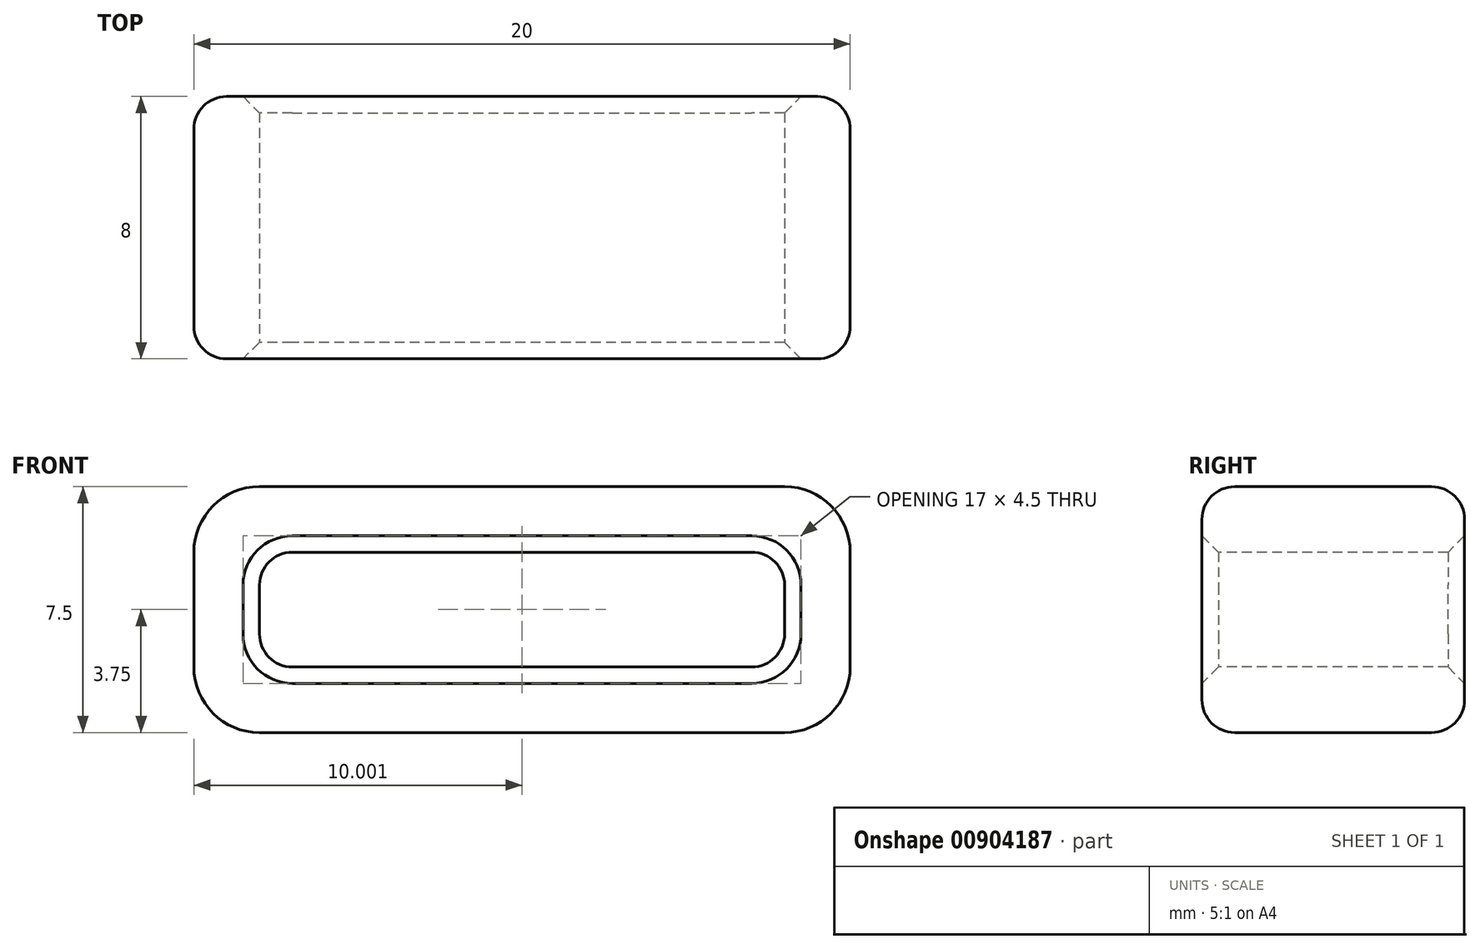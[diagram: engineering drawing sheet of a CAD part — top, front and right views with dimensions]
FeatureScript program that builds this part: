
annotation { "Feature Type Name" : "Feature", "Feature Type Description" : "" }
export const myFeature = defineFeature(function(context is Context, id is Id, definition is map)
    precondition{}
    {
        {
            var Q0;
            Q0=qCreatedBy(makeId("Top.planeOp"),FACE);
            var sketch = newSketch(context, id + "F0", { "sketchPlane" : qUnion([Q0])});
            skLineSegment(sketch, "E0.bottom", {"start": v(5.5, 5.36) * mm, "end": v(25.5, 5.36) * mm});
            skLineSegment(sketch, "E0.top", {"start": v(5.5, -2.64) * mm, "end": v(25.5, -2.64) * mm});
            skLineSegment(sketch, "E0.left", {"start": v(5.5, 5.36) * mm, "end": v(5.5, -2.64) * mm});
            skLineSegment(sketch, "E0.right", {"start": v(25.5, 5.36) * mm, "end": v(25.5, -2.64) * mm});
            skSolve(sketch);
        }
        {
            var Q0;
            Q0 = qSketchRegion(id + "F0", true);
            extrude(context, id + "F1", {"entities" : qUnion([Q0]), "depth" : 7.5 * mm, "offsetDistance" : 25 * mm});
        }
        {
            var Q0;
            Q0=makeQuery(id+"F1.opExtrude","SWEPT_FACE",FACE,{"disambiguationData":[OSD([sQuery(id+"F0.wireOp",EDGE,"E0.top")])]});
            var Q1;
            Q1=makeQuery(id+"F1.opExtrude","SWEPT_BODY",BODY,{"disambiguationData":[OSD([sQuery(id+"F0.wireOp",EDGE,"E0.bottom"),sQuery(id+"F0.wireOp",EDGE,"E0.top"),sQuery(id+"F0.wireOp",EDGE,"E0.left"),sQuery(id+"F0.wireOp",EDGE,"E0.right")])]});
            shell(context, id + "F2", {"entities" : qUnion([Q0]), "parts" : qUnion([Q1]), "thickness" : 2 * mm});
        }
        {
            var Q0;
            Q0=makeQuery(id+"F2.opShell","OFFSET_FACE",FACE,{"disambiguationData":[OSD([sQuery(id+"F0.wireOp",EDGE,"E0.bottom")])]});
            extrude(context, id + "F3", {"entities" : qUnion([Q0]), "operationType" : NewBodyOperationType.REMOVE, "oppositeDirection" : true, "depth" : 25 * mm, "offsetDistance" : 25 * mm});
        }
        {
            var Q0;
            Q0=makeQuery(id+"F1.opExtrude","CAP_EDGE",EDGE,{"disambiguationData":[OSD([sQuery(id+"F0.wireOp",EDGE,"E0.right")])],"isStart":false});
            var Q1;
            Q1=makeQuery(id+"F1.opExtrude","CAP_EDGE",EDGE,{"disambiguationData":[OSD([sQuery(id+"F0.wireOp",EDGE,"E0.right")])],"isStart":true});
            var Q2;
            Q2=makeQuery(id+"F1.opExtrude","CAP_EDGE",EDGE,{"disambiguationData":[OSD([sQuery(id+"F0.wireOp",EDGE,"E0.left")])],"isStart":false});
            var Q3;
            Q3=makeQuery(id+"F1.opExtrude","CAP_EDGE",EDGE,{"disambiguationData":[OSD([sQuery(id+"F0.wireOp",EDGE,"E0.left")])],"isStart":true});
            fillet(context, id + "F4", {"entities" : qUnion([Q0, Q1, Q2, Q3]), "radius" : 2 * mm, "tangentPropagation" : true, "allowEdgeOverflow" : false});
        }
        {
            var Q0;
            {var subQ0=sQuery(id+"F0.wireOp",EDGE,"E0.left");var subQ1=sQuery(id+"F0.wireOp",EDGE,"E0.bottom");Q0=makeQuery(id+"F3.boolean.opBoolean","MERGE",EDGE,{"derivedFrom":[makeQuery(id+"F2.opShell","OFFSET_EDGE",EDGE,{"disambiguationData":[OSD([subQ0]),TDD([makeQuery(id+"F1.opExtrude","CAP_EDGE",EDGE,{"disambiguationData":[OSD([subQ0])],"isStart":false})])]})],"fromTools":[makeQuery(id+"F3.opExtrude","SWEPT_EDGE",EDGE,{"disambiguationData":[OSD([subQ1,subQ0]),TDD([makeQuery(id+"F2.opShell","OFFSET_VERTEX",VERTEX,{"disambiguationData":[OSD([subQ1,subQ0]),TDD([makeQuery(id+"F1.opExtrude","CAP_VERTEX",VERTEX,{"disambiguationData":[OSD([subQ1,subQ0])],"isStart":false})])]})])]})]});}
            var Q1;
            {var subQ0=sQuery(id+"F0.wireOp",EDGE,"E0.left");var subQ1=sQuery(id+"F0.wireOp",EDGE,"E0.bottom");Q1=makeQuery(id+"F3.boolean.opBoolean","MERGE",EDGE,{"derivedFrom":[makeQuery(id+"F2.opShell","OFFSET_EDGE",EDGE,{"disambiguationData":[OSD([subQ0]),TDD([makeQuery(id+"F1.opExtrude","CAP_EDGE",EDGE,{"disambiguationData":[OSD([subQ0])],"isStart":true})])]})],"fromTools":[makeQuery(id+"F3.opExtrude","SWEPT_EDGE",EDGE,{"disambiguationData":[OSD([subQ1,subQ0]),TDD([makeQuery(id+"F2.opShell","OFFSET_VERTEX",VERTEX,{"disambiguationData":[OSD([subQ1,subQ0]),TDD([makeQuery(id+"F1.opExtrude","CAP_VERTEX",VERTEX,{"disambiguationData":[OSD([subQ1,subQ0])],"isStart":true})])]})])]})]});}
            var Q2;
            {var subQ0=sQuery(id+"F0.wireOp",EDGE,"E0.right");var subQ1=sQuery(id+"F0.wireOp",EDGE,"E0.bottom");Q2=makeQuery(id+"F3.boolean.opBoolean","MERGE",EDGE,{"derivedFrom":[makeQuery(id+"F2.opShell","OFFSET_EDGE",EDGE,{"disambiguationData":[OSD([subQ0]),TDD([makeQuery(id+"F1.opExtrude","CAP_EDGE",EDGE,{"disambiguationData":[OSD([subQ0])],"isStart":false})])]})],"fromTools":[makeQuery(id+"F3.opExtrude","SWEPT_EDGE",EDGE,{"disambiguationData":[OSD([subQ1,subQ0]),TDD([makeQuery(id+"F2.opShell","OFFSET_VERTEX",VERTEX,{"disambiguationData":[OSD([subQ1,subQ0]),TDD([makeQuery(id+"F1.opExtrude","CAP_VERTEX",VERTEX,{"disambiguationData":[OSD([subQ1,subQ0])],"isStart":false})])]})])]})]});}
            var Q3;
            {var subQ0=sQuery(id+"F0.wireOp",EDGE,"E0.right");var subQ1=sQuery(id+"F0.wireOp",EDGE,"E0.bottom");Q3=makeQuery(id+"F3.boolean.opBoolean","MERGE",EDGE,{"derivedFrom":[makeQuery(id+"F2.opShell","OFFSET_EDGE",EDGE,{"disambiguationData":[OSD([subQ0]),TDD([makeQuery(id+"F1.opExtrude","CAP_EDGE",EDGE,{"disambiguationData":[OSD([subQ0])],"isStart":true})])]})],"fromTools":[makeQuery(id+"F3.opExtrude","SWEPT_EDGE",EDGE,{"disambiguationData":[OSD([subQ1,subQ0]),TDD([makeQuery(id+"F2.opShell","OFFSET_VERTEX",VERTEX,{"disambiguationData":[OSD([subQ1,subQ0]),TDD([makeQuery(id+"F1.opExtrude","CAP_VERTEX",VERTEX,{"disambiguationData":[OSD([subQ1,subQ0])],"isStart":true})])]})])]})]});}
            fillet(context, id + "F5", {"entities" : qUnion([Q0, Q1, Q2, Q3]), "radius" : 1 * mm, "tangentPropagation" : true, "allowEdgeOverflow" : false});
        }
        {
            var Q0;
            Q0=makeQuery(id+"F1.opExtrude","CAP_EDGE",EDGE,{"disambiguationData":[OSD([sQuery(id+"F0.wireOp",EDGE,"E0.top")])],"isStart":true});
            var Q1;
            Q1=makeQuery(id+"F1.opExtrude","CAP_EDGE",EDGE,{"disambiguationData":[OSD([sQuery(id+"F0.wireOp",EDGE,"E0.bottom")])],"isStart":true});
            fillet(context, id + "F6", {"entities" : qUnion([Q0, Q1]), "radius" : 1 * mm, "tangentPropagation" : true, "allowEdgeOverflow" : false});
        }
        {
            var Q0;
            {var subQ0=sQuery(id+"F0.wireOp",EDGE,"E0.top");Q0=makeQuery(id+"F2.opShell","OFFSET_EDGE",EDGE,{"disambiguationData":[OSD([subQ0]),TDD([makeQuery(id+"F1.opExtrude","CAP_EDGE",EDGE,{"disambiguationData":[OSD([subQ0])],"isStart":false})])]});}
            var Q1;
            {var subQ0=sQuery(id+"F0.wireOp",EDGE,"E0.bottom");Q1=makeQuery(id+"F3.boolean.opBoolean","INTERSECT",EDGE,{"derivedFrom":[makeQuery(id+"F1.opExtrude","SWEPT_FACE",FACE,{"disambiguationData":[OSD([subQ0])]}),makeQuery(id+"F3.opExtrude","SWEPT_FACE",FACE,{"disambiguationData":[OSD([subQ0]),TDD([makeQuery(id+"F2.opShell","OFFSET_EDGE",EDGE,{"disambiguationData":[OSD([subQ0]),TDD([makeQuery(id+"F1.opExtrude","CAP_EDGE",EDGE,{"disambiguationData":[OSD([subQ0])],"isStart":false})])]})])]})]});}
            chamfer(context, id + "F7", {"entities" : qUnion([Q0, Q1]), "width" : .5 * mm, "tangentPropagation" : true});
        }
        {
            var Q0;
            Q0=makeQuery(id+"F1.opExtrude","CAP_FACE",FACE,{"disambiguationData":[OSD([sQuery(id+"F0.wireOp",EDGE,"E0.bottom"),sQuery(id+"F0.wireOp",EDGE,"E0.top"),sQuery(id+"F0.wireOp",EDGE,"E0.left"),sQuery(id+"F0.wireOp",EDGE,"E0.right")])],"isStart":false});
            var sketch = newSketch(context, id + "F8", { "sketchPlane" : qUnion([Q0])});
            skLineSegment(sketch, "E1", {"start": v(8.29, 4.36) * mm, "end": v(8.29, -1.64) * mm});
            skLineSegment(sketch, "E2", {"start": v(8.29, -1.64) * mm, "end": v(9.6, -1.64) * mm});
            skLineSegment(sketch, "E3", {"start": v(9.6, -1.64) * mm, "end": v(9.6, 1.04) * mm});
            skLineSegment(sketch, "E4", {"start": v(9.6, 1.04) * mm, "end": v(10.6, -1.64) * mm});
            skLineSegment(sketch, "E5", {"start": v(10.6, -1.64) * mm, "end": v(12.16, -1.64) * mm});
            skLineSegment(sketch, "E6", {"start": v(12.16, -1.64) * mm, "end": v(10.76, 1.52) * mm});
            skLineSegment(sketch, "E7", {"start": v(10.76, 1.52) * mm, "end": v(12.16, 4.36) * mm});
            skLineSegment(sketch, "E8", {"start": v(12.16, 4.36) * mm, "end": v(10.5, 4.36) * mm});
            skLineSegment(sketch, "E9", {"start": v(8.29, 4.36) * mm, "end": v(9.6, 4.36) * mm});
            skLineSegment(sketch, "E10", {"start": v(9.6, 4.36) * mm, "end": v(9.6, 2.1) * mm});
            skLineSegment(sketch, "E11", {"start": v(9.6, 2.1) * mm, "end": v(10.5, 4.36) * mm});
            skLineSegment(sketch, "E12", {"start": v(12.16, -1.64) * mm, "end": v(12.16, 4.36) * mm});
            skLineSegment(sketch, "E13", {"start": v(12.16, 4.36) * mm, "end": v(16.45, 4.36) * mm});
            skLineSegment(sketch, "E14", {"start": v(16.45, 4.36) * mm, "end": v(16.45, 2.08) * mm});
            skLineSegment(sketch, "E15", {"start": v(16.45, 2.08) * mm, "end": v(15.44, 2.08) * mm});
            skLineSegment(sketch, "E16", {"start": v(15.44, 2.08) * mm, "end": v(15.44, 3.05) * mm});
            skLineSegment(sketch, "E17", {"start": v(15.44, 3.05) * mm, "end": v(13.55, 3.05) * mm});
            skLineSegment(sketch, "E18", {"start": v(13.55, 3.05) * mm, "end": v(13.55, 0) * mm});
            skLineSegment(sketch, "E19", {"start": v(13.55, 0) * mm, "end": v(15.44, 0) * mm});
            skLineSegment(sketch, "E20", {"start": v(15.44, 0) * mm, "end": v(15.44, 0.65) * mm});
            skLineSegment(sketch, "E21", {"start": v(15.44, 0.65) * mm, "end": v(14.31, 0.65) * mm});
            skLineSegment(sketch, "E22", {"start": v(14.31, 0.65) * mm, "end": v(14.31, 1.21) * mm});
            skLineSegment(sketch, "E23", {"start": v(14.31, 1.21) * mm, "end": v(16.45, 1.21) * mm});
            skLineSegment(sketch, "E24", {"start": v(16.45, 1.21) * mm, "end": v(16.45, -1.64) * mm});
            skLineSegment(sketch, "E25", {"start": v(16.45, -1.64) * mm, "end": v(12.16, -1.64) * mm});
            skSolve(sketch);
        }
        {
            var Q0;
            Q0=makeQuery(id+"F8.imprint","IMPRINT",FACE,{"disambiguationData":[TD([[makeQuery(id+"F8.imprint","IMPRINT",EDGE,{"derivedFrom":sQuery(id+"F8.wireOp",EDGE,"E1")}),1.0]])]});
            var Q1;
            Q1=makeQuery(id+"F8.imprint","IMPRINT",FACE,{"disambiguationData":[TD([[makeQuery(id+"F8.imprint","IMPRINT",EDGE,{"derivedFrom":sQuery(id+"F8.wireOp",EDGE,"E12")}),-1.0]])]});
            extrude(context, id + "F9", {"entities" : qUnion([Q0, Q1]), "operationType" : NewBodyOperationType.ADD, "depth" : -1 * mm, "offsetDistance" : 25 * mm});
        }
    });
